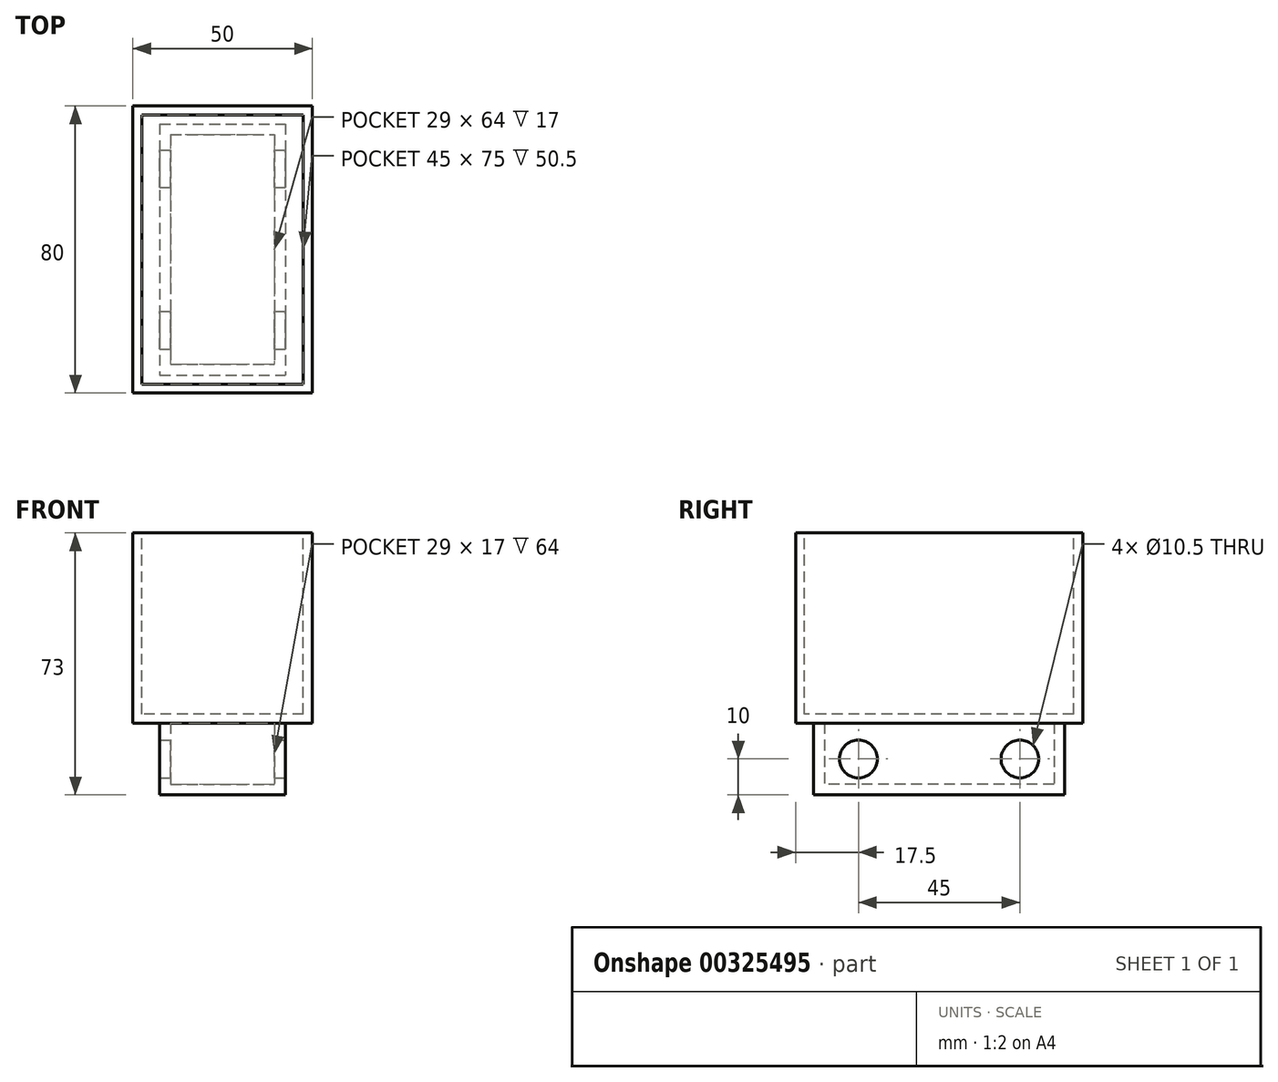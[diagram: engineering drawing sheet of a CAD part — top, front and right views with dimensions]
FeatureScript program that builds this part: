
annotation { "Feature Type Name" : "Feature", "Feature Type Description" : "" }
export const myFeature = defineFeature(function(context is Context, id is Id, definition is map)
    precondition{}
    {
        {
            var Q0;
            Q0=qCreatedBy(makeId("Right.planeOp"),FACE);
            var sketch = newSketch(context, id + "F0", { "sketchPlane" : qUnion([Q0])});
            skLineSegment(sketch, "E0.bottom", {"start": v(35, 10) * mm, "end": v(-35, 10) * mm});
            skLineSegment(sketch, "E0.top", {"start": v(35, -10) * mm, "end": v(-35, -10) * mm});
            skLineSegment(sketch, "E0.left", {"start": v(35, 10) * mm, "end": v(35, -10) * mm});
            skLineSegment(sketch, "E0.right", {"start": v(-35, 10) * mm, "end": v(-35, -10) * mm});
            skPoint(sketch, "E0.middle", {"position": v(0, 0) * mm});
            skCircle(sketch, "E1", {"center": v(-22.5, 0) * mm, "radius": 5.25 * mm});
            skCircle(sketch, "E2", {"center": v(22.5, 0) * mm, "radius": 5.25 * mm});
            skLineSegment(sketch, "E3", {"start": v(0, 10) * mm, "end": v(0, -10) * mm, "construction": true});
            skLineSegment(sketch, "E4", {"start": v(35, 0) * mm, "end": v(-35, 0) * mm, "construction": true});
            skSolve(sketch);
        }
        {
            var Q0;
            Q0 = qSketchRegion(id + "F0", true);
            extrude(context, id + "F1", {"entities" : qUnion([Q0]), "endBound" : BoundingType.SYMMETRIC, "oppositeDirection" : true, "depth" : 35 * mm});
        }
        {
            var Q0;
            Q0=makeQuery(id+"F1.opExtrude","SWEPT_FACE",FACE,{"disambiguationData":[OSD([sQuery(id+"F0.wireOp",EDGE,"E0.bottom")])]});
            var Q1;
            Q1=makeQuery(id+"F1.opExtrude","SWEPT_FACE",FACE,{"disambiguationData":[OSD([sQuery(id+"F0.wireOp",EDGE,"E1")])]});
            var Q2;
            Q2=makeQuery(id+"F1.opExtrude","SWEPT_FACE",FACE,{"disambiguationData":[OSD([sQuery(id+"F0.wireOp",EDGE,"E2")])]});
            var Q3;
            Q3=makeQuery(id+"F1.opExtrude","SWEPT_BODY",BODY,{"disambiguationData":[OSD([sQuery(id+"F0.wireOp",EDGE,"E0.bottom"),sQuery(id+"F0.wireOp",EDGE,"E0.top"),sQuery(id+"F0.wireOp",EDGE,"E0.left"),sQuery(id+"F0.wireOp",EDGE,"E0.right"),sQuery(id+"F0.wireOp",EDGE,"E1"),sQuery(id+"F0.wireOp",EDGE,"E2")])]});
            shell(context, id + "F2", {"entities" : qUnion([Q0, Q1, Q2]), "parts" : qUnion([Q3]), "thickness" : 3 * mm});
        }
        {
            var Q0;
            Q0=qCreatedBy(makeId("Right.planeOp"),FACE);
            var sketch = newSketch(context, id + "F3", { "sketchPlane" : qUnion([Q0])});
            skLineSegment(sketch, "E5.0", {"start": v(35, 10) * mm, "end": v(-35, 10) * mm, "construction": true});
            skLineSegment(sketch, "E6.bottom", {"start": v(40, 10) * mm, "end": v(-40, 10) * mm});
            skLineSegment(sketch, "E6.top", {"start": v(40, 63) * mm, "end": v(-40, 63) * mm});
            skLineSegment(sketch, "E6.left", {"start": v(40, 10) * mm, "end": v(40, 63) * mm});
            skLineSegment(sketch, "E6.right", {"start": v(-40, 10) * mm, "end": v(-40, 63) * mm});
            skPoint(sketch, "E6.middle", {"position": v(0, 36.5) * mm});
            skSolve(sketch);
        }
        {
            var Q0;
            Q0 = qSketchRegion(id + "F3", true);
            extrude(context, id + "F4", {"entities" : qUnion([Q0]), "operationType" : NewBodyOperationType.ADD, "endBound" : BoundingType.SYMMETRIC, "depth" : 50 * mm});
        }
        {
            var Q0;
            Q0=makeQuery(id+"F4.opExtrude","SWEPT_FACE",FACE,{"disambiguationData":[OSD([sQuery(id+"F3.wireOp",EDGE,"E6.top")])]});
            shell(context, id + "F5", {"entities" : qUnion([Q0]), "thickness" : 2.5 * mm});
        }
    });
